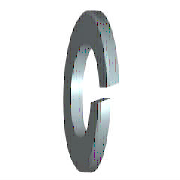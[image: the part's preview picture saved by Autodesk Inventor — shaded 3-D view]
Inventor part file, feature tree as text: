
AUTODESK INVENTOR PART (.ipt)
format: ipt  version: 2021 (Build 250183000, 183)  size: 126,976 bytes
history: native  units: mm (DEFAULTED — no unit token found)
features: sketch x2, extrude x1, other x1, plane x1
ambient origin geometry x6: Origin, YZ Plane, X Axis, Y Axis, Z Axis, Center Point
bodies: Solid1 (feature_tree), Body (feature_tree)
feature tree (5):
  extrude  "Cut"  Depth=7.6mm
  other  "Work Axis1"
  plane  "Work Plane1"
  sketch  "Sketch1"  dims[d0=4.1mm d1=7.6mm]
  sketch  "Sketch2"  dims[d2=1.0mm d3=0.0mm d4=0.2mm d5=0.2mm d6=12.217305mm d7=1.0mm d8=0.0mm d9=0.0mm d10=0.0mm d11=0.0mm d12=0.0mm]
